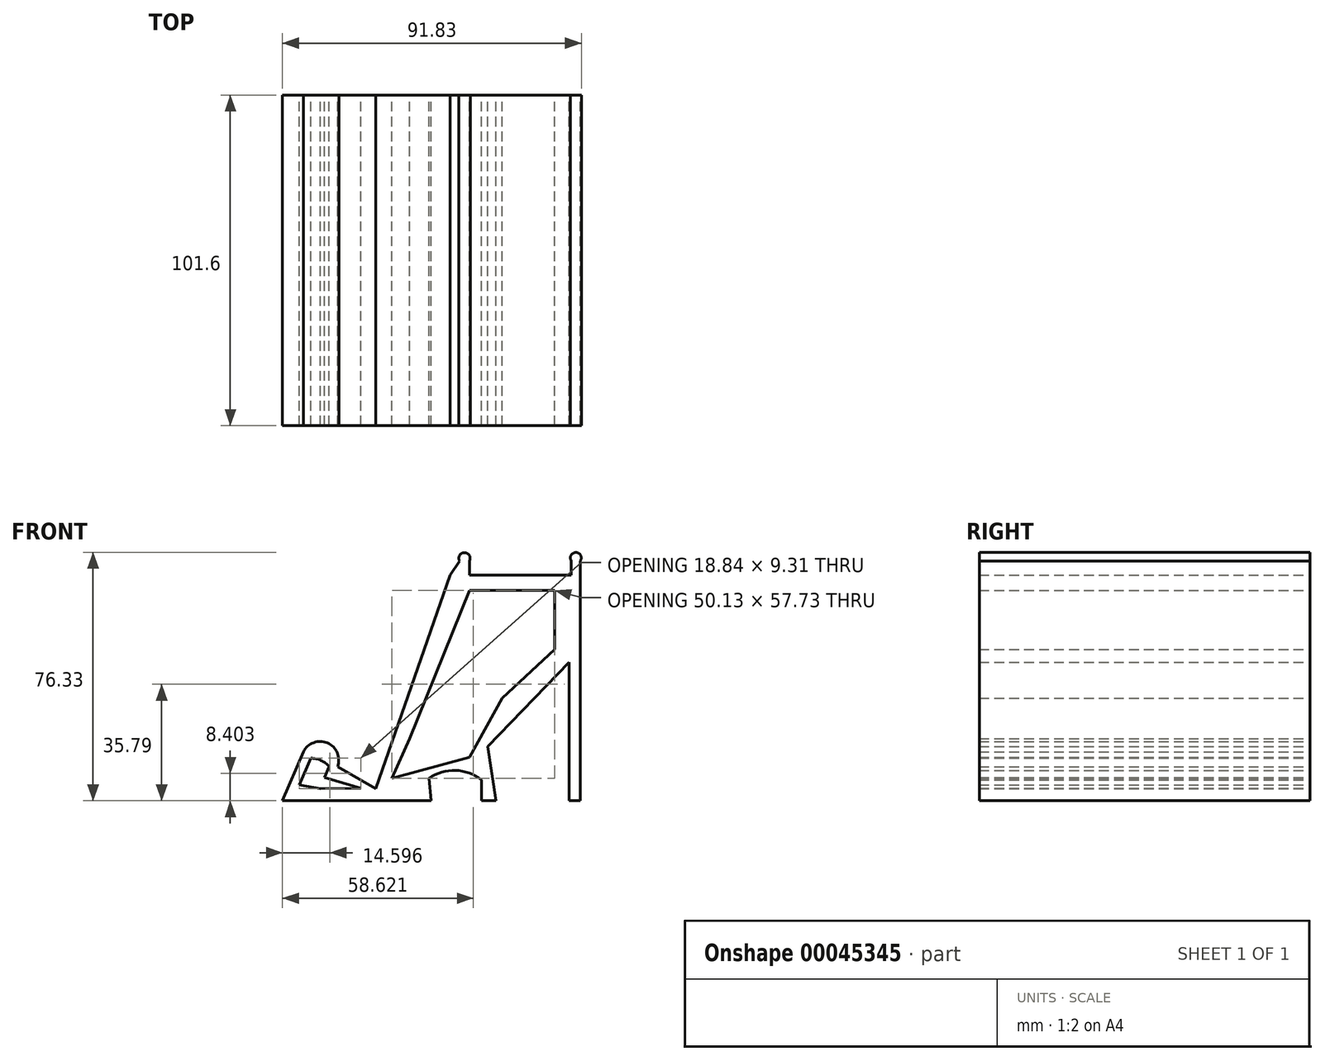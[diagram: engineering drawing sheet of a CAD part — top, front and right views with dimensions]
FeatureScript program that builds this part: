
annotation { "Feature Type Name" : "Feature", "Feature Type Description" : "" }
export const myFeature = defineFeature(function(context is Context, id is Id, definition is map)
    precondition{}
    {
        {
            var Q0;
            Q0=qCreatedBy(makeId("Front.planeOp"),FACE);
            var sketch = newSketch(context, id + "F0", { "sketchPlane" : qUnion([Q0])});
            skLineSegment(sketch, "E0", {"start": v(-30.2, 3.47) * mm, "end": v(-11.83, 56.06) * mm});
            skPoint(sketch, "E1.end.orphan", {"position": v(-31.27, 56.06) * mm});
            skLineSegment(sketch, "E2", {"start": v(-41.7, 10.96) * mm, "end": v(-40.57, 13.91) * mm});
            skLineSegment(sketch, "E3", {"start": v(-51.07, 18.41) * mm, "end": v(-57.47, 3.47) * mm});
            skLineSegment(sketch, "E4", {"start": v(-57.47, 3.47) * mm, "end": v(-30.2, 3.47) * mm});
            skLineSegment(sketch, "E5", {"start": v(-30.2, 3.47) * mm, "end": v(-17.64, 3.47) * mm});
            skLineSegment(sketch, "E6", {"start": v(-43.83, 7.22) * mm, "end": v(-42.77, 7.22) * mm});
            skPoint(sketch, "E6.startSnap0", {"position": v(-42.77, 7.22) * mm});
            skLineSegment(sketch, "E7", {"start": v(-40.57, 13.91) * mm, "end": v(-28.88, 7.22) * mm});
            skArc(sketch, "E8", {"start": v(8.17, 3.47) * mm, "mid": v(-4.73, 12.77) * mm, "end": v(-17.64, 3.47) * mm});
            skLineSegment(sketch, "E9", {"start": v(3.64, 9.9) * mm, "end": v(3.64, 3.47) * mm});
            skLineSegment(sketch, "E10", {"start": v(8.17, 3.47) * mm, "end": v(3.64, 3.47) * mm});
            skLineSegment(sketch, "E11", {"start": v(-17.64, 3.47) * mm, "end": v(-11.83, 3.47) * mm});
            skLineSegment(sketch, "E12", {"start": v(-12.42, 10.4) * mm, "end": v(-11.83, 3.47) * mm});
            skLineSegment(sketch, "E13", {"start": v(34.09, 49.73) * mm, "end": v(34.09, 56.36) * mm});
            skLineSegment(sketch, "E14", {"start": v(5.6, 20.15) * mm, "end": v(30.57, 46.08) * mm});
            skPoint(sketch, "E15.orphan", {"position": v(-34.65, 29.3) * mm});
            skPoint(sketch, "E16.orphan", {"position": v(-38.18, 20.13) * mm});
            skArc(sketch, "E17", {"start": v(-40.57, 13.91) * mm, "mid": v(-43.65, 21.22) * mm, "end": v(-51.07, 18.41) * mm});
            skPoint(sketch, "E18", {"position": v(-57.47, 3.47) * mm});
            skPoint(sketch, "E19", {"position": v(34.09, 3.47) * mm});
            skLineSegment(sketch, "E20", {"start": v(34.09, 49.73) * mm, "end": v(34.09, 3.47) * mm});
            skLineSegment(sketch, "E21", {"start": v(30.57, 46.08) * mm, "end": v(30.57, 3.47) * mm});
            skLineSegment(sketch, "E22", {"start": v(30.57, 3.47) * mm, "end": v(34.09, 3.47) * mm});
            skLineSegment(sketch, "E23", {"start": v(5.6, 20.15) * mm, "end": v(8.17, 3.47) * mm});
            skPoint(sketch, "E24.orphan", {"position": v(-43.83, 3.47) * mm});
            skLineSegment(sketch, "E25", {"start": v(-11.83, 56.06) * mm, "end": v(-5.96, 72.88) * mm});
            skLineSegment(sketch, "E26", {"start": v(-5.96, 72.88) * mm, "end": v(34.09, 72.88) * mm});
            skLineSegment(sketch, "E27", {"start": v(34.09, 72.88) * mm, "end": v(34.09, 56.36) * mm});
            skLineSegment(sketch, "E28", {"start": v(-3.1, 77.2) * mm, "end": v(-3.1, 72.88) * mm});
            skLineSegment(sketch, "E29", {"start": v(34.09, 72.88) * mm, "end": v(34.09, 77.2) * mm});
            skLineSegment(sketch, "E30", {"start": v(34.09, 77.2) * mm, "end": v(31.27, 77.2) * mm});
            skLineSegment(sketch, "E31", {"start": v(31.27, 77.2) * mm, "end": v(31.27, 72.88) * mm});
            skArc(sketch, "E32", {"start": v(34.09, 77.2) * mm, "mid": v(32.68, 79.8) * mm, "end": v(31.27, 77.2) * mm});
            skPoint(sketch, "E33.startSnap0", {"position": v(-8.9, 64.47) * mm});
            skLineSegment(sketch, "E34", {"start": v(26.22, 64.47) * mm, "end": v(26.22, 54) * mm});
            skArc(sketch, "E35", {"start": v(-41.7, 10.96) * mm, "mid": v(-45.84, 15.94) * mm, "end": v(-52.3, 15.55) * mm});
            skLineSegment(sketch, "E36", {"start": v(-48.76, 16.53) * mm, "end": v(-52.3, 8.28) * mm});
            skPoint(sketch, "E37.endSnap0", {"position": v(-41.14, 12.44) * mm});
            skLineSegment(sketch, "E38", {"start": v(-43.15, 13.91) * mm, "end": v(-45.9, 7.22) * mm});
            skLineSegment(sketch, "E39", {"start": v(-45.9, 7.22) * mm, "end": v(-52.3, 8.28) * mm});
            skLineSegment(sketch, "E40", {"start": v(0, 72.88) * mm, "end": v(0, 77.2) * mm});
            skLineSegment(sketch, "E41", {"start": v(0, 77.2) * mm, "end": v(-3.1, 77.2) * mm});
            skArc(sketch, "E42", {"start": v(0, 77.2) * mm, "mid": v(-1.55, 79.74) * mm, "end": v(-3.1, 77.2) * mm});
            skLineSegment(sketch, "E43", {"start": v(-5.96, 72.88) * mm, "end": v(-3.1, 77.2) * mm});
            skLineSegment(sketch, "E44", {"start": v(0, 16.8) * mm, "end": v(0, 20.54) * mm});
            skLineSegment(sketch, "E45", {"start": v(0, 64.47) * mm, "end": v(0, 68.13) * mm});
            skLineSegment(sketch, "E46", {"start": v(0, 68.13) * mm, "end": v(26.22, 68.13) * mm});
            skLineSegment(sketch, "E47", {"start": v(26.22, 68.13) * mm, "end": v(26.22, 64.47) * mm});
            skLineSegment(sketch, "E48", {"start": v(9.99, 35) * mm, "end": v(26.22, 49.96) * mm});
            skLineSegment(sketch, "E49", {"start": v(26.22, 49.96) * mm, "end": v(26.22, 54) * mm});
            skLineSegment(sketch, "E50", {"start": v(0, 68.13) * mm, "end": v(-18.46, 22.56) * mm});
            skLineSegment(sketch, "E51", {"start": v(-18.46, 22.56) * mm, "end": v(-23.91, 10.4) * mm});
            skPoint(sketch, "E51.endSnap0", {"position": v(-23.91, 3.47) * mm});
            skLineSegment(sketch, "E52", {"start": v(-23.91, 10.4) * mm, "end": v(0, 16.8) * mm});
            skLineSegment(sketch, "E53", {"start": v(0, 16.8) * mm, "end": v(9.99, 35) * mm});
            skPoint(sketch, "E54", {"position": v(-44.53, 9.37) * mm});
            skPoint(sketch, "E54.positionSnap0", {"position": v(-44.53, 10.57) * mm});
            skLineSegment(sketch, "E55", {"start": v(-44.53, 10.57) * mm, "end": v(-33.45, 7.28) * mm});
            skLineSegment(sketch, "E56", {"start": v(-45.9, 7.22) * mm, "end": v(-33.45, 7.28) * mm});
            skSolve(sketch);
        }
        {
            var Q0;
            Q0 = qSketchRegion(id + "F0", true);
            extrude(context, id + "F1", {"entities" : qUnion([Q0]), "depth" : 101.6 * mm});
        }
    });
